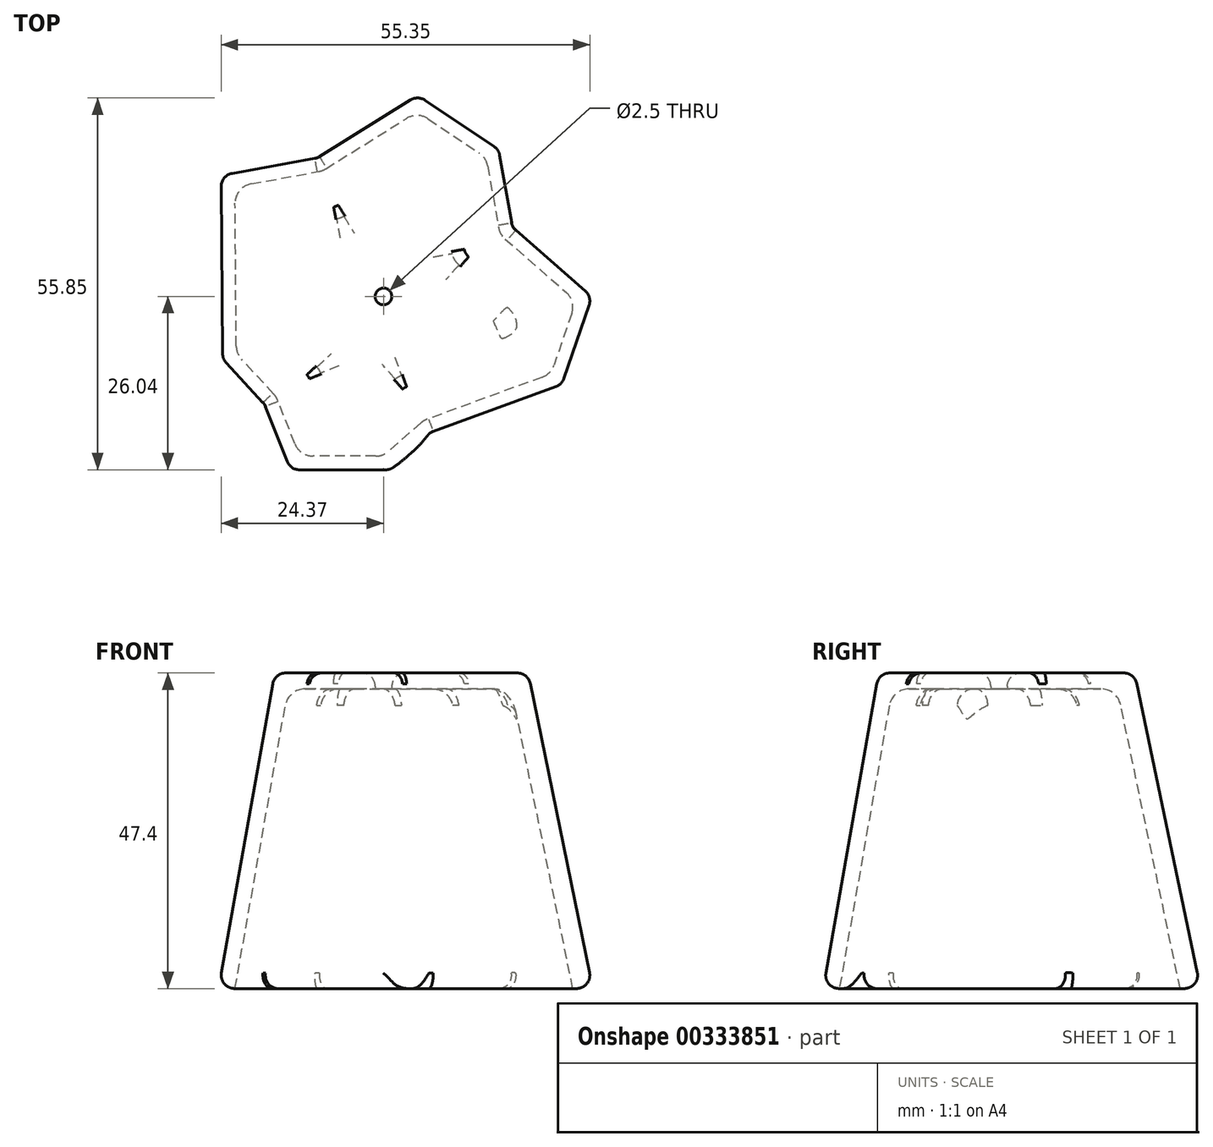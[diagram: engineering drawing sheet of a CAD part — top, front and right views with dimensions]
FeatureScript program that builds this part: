
annotation { "Feature Type Name" : "Feature", "Feature Type Description" : "" }
export const myFeature = defineFeature(function(context is Context, id is Id, definition is map)
    precondition{}
    {
        {
            var Q0;
            Q0=qCreatedBy(makeId("Top.planeOp"),FACE);
            var sketch = newSketch(context, id + "F0", { "sketchPlane" : qUnion([Q0])});
            skLineSegment(sketch, "E0", {"start": v(-16.1, -15.08) * mm, "end": v(-22.1, -8.58) * mm});
            skLineSegment(sketch, "E1", {"start": v(-22.1, -8.58) * mm, "end": v(-22.32, 16.48) * mm});
            skLineSegment(sketch, "E2", {"start": v(-22.32, 16.48) * mm, "end": v(-9.18, 18.86) * mm});
            skLineSegment(sketch, "E3", {"start": v(-9.18, 18.86) * mm, "end": v(5.1, 27.75) * mm});
            skLineSegment(sketch, "E4", {"start": v(5.1, 27.75) * mm, "end": v(15.42, 20.84) * mm});
            skLineSegment(sketch, "E5", {"start": v(15.42, 20.84) * mm, "end": v(17.46, 9.33) * mm});
            skLineSegment(sketch, "E6", {"start": v(17.46, 9.33) * mm, "end": v(28.92, -0.68) * mm});
            skLineSegment(sketch, "E7", {"start": v(28.92, -0.68) * mm, "end": v(25.15, -11.63) * mm});
            skLineSegment(sketch, "E8", {"start": v(25.15, -11.63) * mm, "end": v(6.05, -18.6) * mm});
            skLineSegment(sketch, "E9", {"start": v(6.05, -18.6) * mm, "end": v(-0.08, -23.98) * mm});
            skLineSegment(sketch, "E10", {"start": v(-0.08, -23.98) * mm, "end": v(-12.57, -23.98) * mm});
            skLineSegment(sketch, "E11", {"start": v(-12.57, -23.98) * mm, "end": v(-16.1, -15.08) * mm});
            skSolve(sketch);
        }
        {
            var Q0;
            Q0=makeQuery(id+"F0.imprint","IMPRINT",FACE,{"disambiguationData":[TD([[makeQuery(id+"F0.imprint","IMPRINT",EDGE,{"derivedFrom":sQuery(id+"F0.wireOp",EDGE,"E0")}),-1.0]])]});
            extrude(context, id + "F1", {"entities" : qUnion([Q0]), "depth" : 45 * mm, "hasDraft" : true, "draftAngle" : 10 * degree, "draftPullDirection" : true});
        }
        {
            var Q0;
            Q0=makeQuery(id+"F1.opExtrude","CAP_FACE",FACE,{"disambiguationData":[OSD([sQuery(id+"F0.wireOp",EDGE,"vM3dCzA2-2G0Q-ovcB-lurY-vvAaln08yTSb")])],"isStart":true});
            var Q1;
            Q1=makeQuery(id+"F1.opExtrude","CAP_FACE",FACE,{"disambiguationData":[OSD([sQuery(id+"F0.wireOp",EDGE,"E0"),sQuery(id+"F0.wireOp",EDGE,"E1"),sQuery(id+"F0.wireOp",EDGE,"E2"),sQuery(id+"F0.wireOp",EDGE,"E3"),sQuery(id+"F0.wireOp",EDGE,"E4"),sQuery(id+"F0.wireOp",EDGE,"E5"),sQuery(id+"F0.wireOp",EDGE,"E6"),sQuery(id+"F0.wireOp",EDGE,"E7"),sQuery(id+"F0.wireOp",EDGE,"E8"),sQuery(id+"F0.wireOp",EDGE,"E9"),sQuery(id+"F0.wireOp",EDGE,"E10"),sQuery(id+"F0.wireOp",EDGE,"E11")])],"isStart":true});
            shell(context, id + "F2", {"entities" : qUnion([Q0, Q1]), "thickness" : 2.4 * mm, "oppositeDirection" : true});
        }
        {
            var Q0;
            Q0=makeQuery(id+"F2.opShell","OFFSET_FACE",FACE,{"disambiguationData":[OSD([sQuery(id+"F0.wireOp",EDGE,"E0"),sQuery(id+"F0.wireOp",EDGE,"E1"),sQuery(id+"F0.wireOp",EDGE,"E2"),sQuery(id+"F0.wireOp",EDGE,"E3"),sQuery(id+"F0.wireOp",EDGE,"E4"),sQuery(id+"F0.wireOp",EDGE,"E5"),sQuery(id+"F0.wireOp",EDGE,"E6"),sQuery(id+"F0.wireOp",EDGE,"E7"),sQuery(id+"F0.wireOp",EDGE,"E8"),sQuery(id+"F0.wireOp",EDGE,"E9"),sQuery(id+"F0.wireOp",EDGE,"E10"),sQuery(id+"F0.wireOp",EDGE,"E11")])]});
            var Q1;
            Q1=makeQuery(id+"F2.opShell","OFFSET_EDGE",EDGE,{"disambiguationData":[OSD([sQuery(id+"F0.wireOp",EDGE,"E5"),sQuery(id+"F0.wireOp",EDGE,"E6")])]});
            var Q2;
            Q2=makeQuery(id+"F2.opShell","OFFSET_EDGE",EDGE,{"disambiguationData":[OSD([sQuery(id+"F0.wireOp",EDGE,"E6"),sQuery(id+"F0.wireOp",EDGE,"E7")])]});
            var Q3;
            Q3=makeQuery(id+"F2.opShell","OFFSET_EDGE",EDGE,{"disambiguationData":[OSD([sQuery(id+"F0.wireOp",EDGE,"E7"),sQuery(id+"F0.wireOp",EDGE,"E8")])]});
            var Q4;
            Q4=makeQuery(id+"F2.opShell","OFFSET_EDGE",EDGE,{"disambiguationData":[OSD([sQuery(id+"F0.wireOp",EDGE,"E8"),sQuery(id+"F0.wireOp",EDGE,"E9")])]});
            var Q5;
            Q5=makeQuery(id+"F2.opShell","OFFSET_EDGE",EDGE,{"disambiguationData":[OSD([sQuery(id+"F0.wireOp",EDGE,"E9"),sQuery(id+"F0.wireOp",EDGE,"E10")])]});
            var Q6;
            Q6=makeQuery(id+"F2.opShell","OFFSET_EDGE",EDGE,{"disambiguationData":[OSD([sQuery(id+"F0.wireOp",EDGE,"E4"),sQuery(id+"F0.wireOp",EDGE,"E5")])]});
            var Q7;
            Q7=makeQuery(id+"F2.opShell","OFFSET_EDGE",EDGE,{"disambiguationData":[OSD([sQuery(id+"F0.wireOp",EDGE,"E3"),sQuery(id+"F0.wireOp",EDGE,"E4")])]});
            var Q8;
            Q8=makeQuery(id+"F2.opShell","OFFSET_EDGE",EDGE,{"disambiguationData":[OSD([sQuery(id+"F0.wireOp",EDGE,"E2"),sQuery(id+"F0.wireOp",EDGE,"E3")])]});
            var Q9;
            Q9=makeQuery(id+"F2.opShell","OFFSET_EDGE",EDGE,{"disambiguationData":[OSD([sQuery(id+"F0.wireOp",EDGE,"E1"),sQuery(id+"F0.wireOp",EDGE,"E2")])]});
            var Q10;
            Q10=makeQuery(id+"F2.opShell","OFFSET_EDGE",EDGE,{"disambiguationData":[OSD([sQuery(id+"F0.wireOp",EDGE,"E0"),sQuery(id+"F0.wireOp",EDGE,"E1")])]});
            var Q11;
            Q11=makeQuery(id+"F2.opShell","OFFSET_EDGE",EDGE,{"disambiguationData":[OSD([sQuery(id+"F0.wireOp",EDGE,"E0"),sQuery(id+"F0.wireOp",EDGE,"E11")])]});
            var Q12;
            Q12=makeQuery(id+"F2.opShell","OFFSET_EDGE",EDGE,{"disambiguationData":[OSD([sQuery(id+"F0.wireOp",EDGE,"E10"),sQuery(id+"F0.wireOp",EDGE,"E11")])]});
            fillet(context, id + "F3", {"entities" : qUnion([Q0, Q1, Q2, Q3, Q4, Q5, Q6, Q7, Q8, Q9, Q10, Q11, Q12]), "radius" : 3 * mm, "tangentPropagation" : true, "allowEdgeOverflow" : false});
        }
        {
            var Q0;
            Q0=qCreatedBy(makeId("Top.planeOp"),FACE);
            var sketch = newSketch(context, id + "F4", { "sketchPlane" : qUnion([Q0])});
            skCircle(sketch, "E12", {"center": v(0, 0) * mm, "radius": 1.25 * mm});
            skSolve(sketch);
        }
        {
            var Q0;
            Q0 = qSketchRegion(id + "F4", true);
            extrude(context, id + "F5", {"entities" : qUnion([Q0]), "operationType" : NewBodyOperationType.REMOVE, "depth" : 1000 * mm});
        }
        {
            var Q0;
            Q0=makeQuery(id+"F1.opExtrude","CAP_FACE",FACE,{"disambiguationData":[OSD([sQuery(id+"F0.wireOp",EDGE,"E0"),sQuery(id+"F0.wireOp",EDGE,"E1"),sQuery(id+"F0.wireOp",EDGE,"E2"),sQuery(id+"F0.wireOp",EDGE,"E3"),sQuery(id+"F0.wireOp",EDGE,"E4"),sQuery(id+"F0.wireOp",EDGE,"E5"),sQuery(id+"F0.wireOp",EDGE,"E6"),sQuery(id+"F0.wireOp",EDGE,"E7"),sQuery(id+"F0.wireOp",EDGE,"E8"),sQuery(id+"F0.wireOp",EDGE,"E9"),sQuery(id+"F0.wireOp",EDGE,"E10"),sQuery(id+"F0.wireOp",EDGE,"E11")])],"isStart":false});
            var Q1;
            Q1=makeQuery(id+"F1.opExtrude","SWEPT_FACE",FACE,{"disambiguationData":[OSD([sQuery(id+"F0.wireOp",EDGE,"E1")])]});
            var Q2;
            Q2=makeQuery(id+"F1.opExtrude","SWEPT_FACE",FACE,{"disambiguationData":[OSD([sQuery(id+"F0.wireOp",EDGE,"E2")])]});
            var Q3;
            Q3=makeQuery(id+"F1.opExtrude","SWEPT_FACE",FACE,{"disambiguationData":[OSD([sQuery(id+"F0.wireOp",EDGE,"E3")])]});
            var Q4;
            Q4=makeQuery(id+"F1.opExtrude","SWEPT_FACE",FACE,{"disambiguationData":[OSD([sQuery(id+"F0.wireOp",EDGE,"E4")])]});
            var Q5;
            Q5=makeQuery(id+"F1.opExtrude","SWEPT_FACE",FACE,{"disambiguationData":[OSD([sQuery(id+"F0.wireOp",EDGE,"E5")])]});
            var Q6;
            Q6=makeQuery(id+"F1.opExtrude","SWEPT_FACE",FACE,{"disambiguationData":[OSD([sQuery(id+"F0.wireOp",EDGE,"E6")])]});
            var Q7;
            Q7=makeQuery(id+"F1.opExtrude","SWEPT_FACE",FACE,{"disambiguationData":[OSD([sQuery(id+"F0.wireOp",EDGE,"E7")])]});
            var Q8;
            Q8=makeQuery(id+"F1.opExtrude","SWEPT_FACE",FACE,{"disambiguationData":[OSD([sQuery(id+"F0.wireOp",EDGE,"E8")])]});
            var Q9;
            Q9=makeQuery(id+"F1.opExtrude","SWEPT_FACE",FACE,{"disambiguationData":[OSD([sQuery(id+"F0.wireOp",EDGE,"E11")])]});
            var Q10;
            Q10=makeQuery(id+"F1.opExtrude","SWEPT_FACE",FACE,{"disambiguationData":[OSD([sQuery(id+"F0.wireOp",EDGE,"E0")])]});
            var Q11;
            Q11=makeQuery(id+"F1.opExtrude","SWEPT_FACE",FACE,{"disambiguationData":[OSD([sQuery(id+"F0.wireOp",EDGE,"E10")])]});
            fillet(context, id + "F6", {"entities" : qUnion([Q0, Q1, Q2, Q3, Q4, Q5, Q6, Q7, Q8, Q9, Q10, Q11]), "radius" : 2 * mm, "tangentPropagation" : true, "allowEdgeOverflow" : false});
        }
    });
